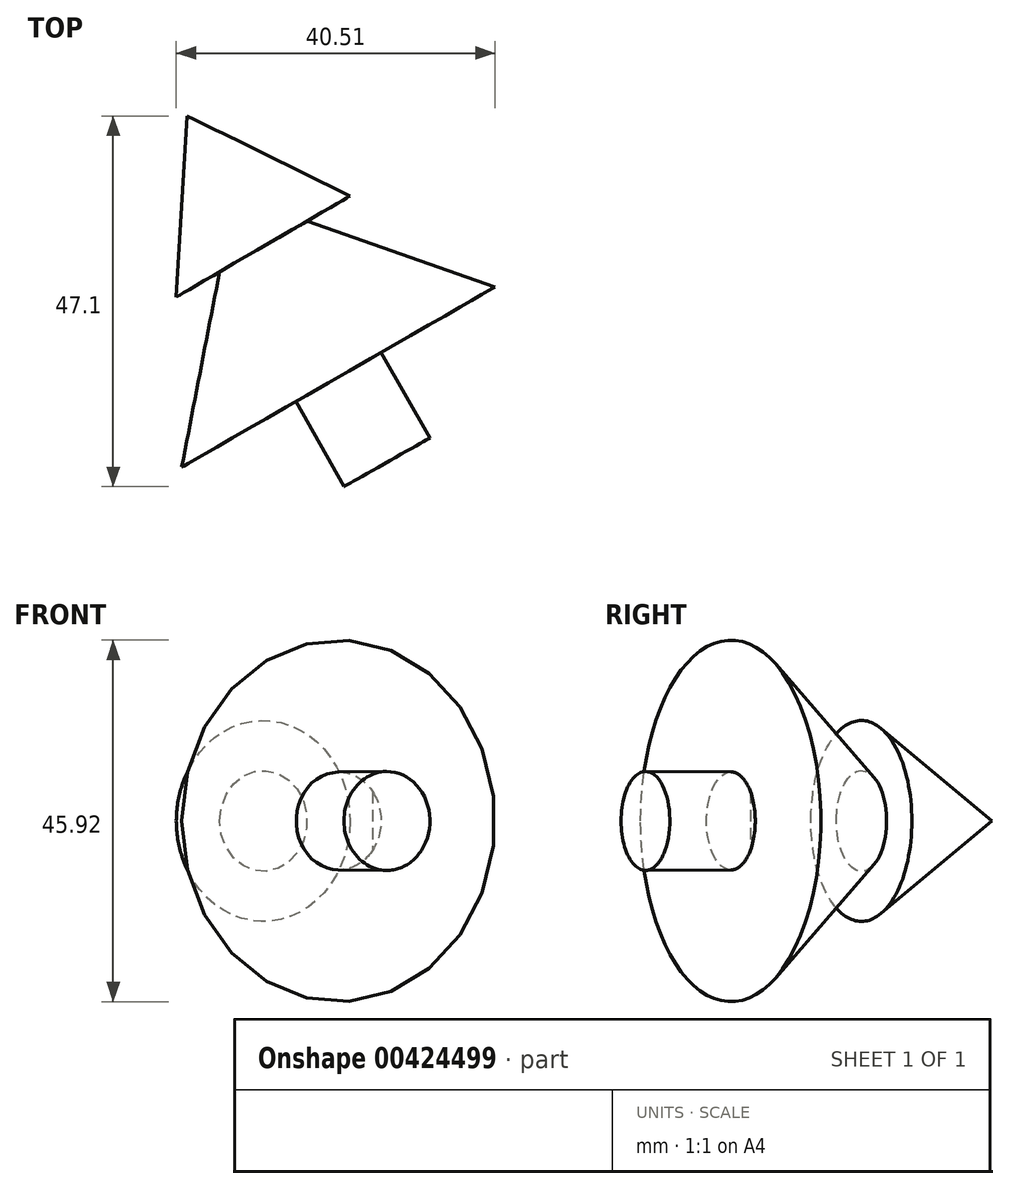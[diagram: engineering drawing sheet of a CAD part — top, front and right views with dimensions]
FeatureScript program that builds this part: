
annotation { "Feature Type Name" : "Feature", "Feature Type Description" : "" }
export const myFeature = defineFeature(function(context is Context, id is Id, definition is map)
    precondition{}
    {
        {
            var Q0;
            Q0=qCreatedBy(makeId("Top.planeOp"),FACE);
            var sketch = newSketch(context, id + "F0", { "sketchPlane" : qUnion([Q0])});
            skLineSegment(sketch, "E0", {"start": v(0, 0) * mm, "end": v(9.64, -16.59) * mm});
            skLineSegment(sketch, "E1", {"start": v(9.64, -16.59) * mm, "end": v(20.67, -10.17) * mm});
            skLineSegment(sketch, "E2", {"start": v(20.67, -10.17) * mm, "end": v(0, 0) * mm});
            skSolve(sketch);
        }
        {
            var Q0;
            Q0 = qSketchRegion(id + "F0", true);
            var Q1;
            Q1=sQuery(id+"F0.wireOp",EDGE,"E0");
            revolve(context, id + "F1", {"entities" : qUnion([Q0]), "axis" : qUnion([Q1]), "revolveType" : RevolveType.FULL});
        }
        {
            var Q0;
            Q0=qCreatedBy(makeId("Top.planeOp"),FACE);
            var sketch = newSketch(context, id + "F2", { "sketchPlane" : qUnion([Q0])});
            skLineSegment(sketch, "E3", {"start": v(9.66, -16.58) * mm, "end": v(15.2, -13.39) * mm});
            skLineSegment(sketch, "E4", {"start": v(9.66, -16.58) * mm, "end": v(19.2, -33.17) * mm});
            skLineSegment(sketch, "E5", {"start": v(19.2, -33.17) * mm, "end": v(39.1, -21.72) * mm});
            skLineSegment(sketch, "E6", {"start": v(39.1, -21.72) * mm, "end": v(15.2, -13.39) * mm});
            skSolve(sketch);
        }
        {
            var Q0;
            Q0=qCreatedBy(makeId("Top.planeOp"),FACE);
            var sketch = newSketch(context, id + "F3", { "sketchPlane" : qUnion([Q0])});
            skLineSegment(sketch, "E7", {"start": v(19.2, -33.14) * mm, "end": v(25.36, -44) * mm});
            skLineSegment(sketch, "E8", {"start": v(25.36, -44) * mm, "end": v(30.82, -40.9) * mm});
            skLineSegment(sketch, "E9", {"start": v(19.2, -33.14) * mm, "end": v(24.61, -30.06) * mm});
            skLineSegment(sketch, "E10", {"start": v(24.61, -30.06) * mm, "end": v(30.82, -40.9) * mm});
            skSolve(sketch);
        }
        {
            var Q0;
            Q0 = qSketchRegion(id + "F2", true);
            var Q1;
            Q1=sQuery(id+"F2.wireOp",EDGE,"E4");
            revolve(context, id + "F4", {"entities" : qUnion([Q0]), "axis" : qUnion([Q1]), "revolveType" : RevolveType.FULL});
        }
        {
            var Q0;
            Q0 = qSketchRegion(id + "F3", true);
            var Q1;
            Q1=sQuery(id+"F3.wireOp",EDGE,"E7");
            revolve(context, id + "F5", {"operationType" : NewBodyOperationType.ADD, "entities" : qUnion([Q0]), "axis" : qUnion([Q1]), "revolveType" : RevolveType.FULL});
        }
    });
